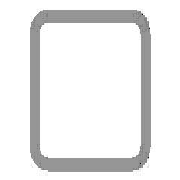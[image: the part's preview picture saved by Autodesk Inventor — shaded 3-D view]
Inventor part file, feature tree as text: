
AUTODESK INVENTOR PART (.ipt)
format: ipt  version: 2024 (Build 280153000, 153)  size: 137,216 bytes
history: native  units: mm (DEFAULTED — no unit token found)
features: other x4, plane x3, split x2, extrude x1, sketch x1
ambient origin geometry x8: Origin, YZ Plane, XZ Plane, XY Plane, X Axis, Y Axis, Z Axis, Center Point
bodies: Solid1 (feature_tree)
feature tree (11):
  parser-record x1  (decoder bookkeeping rows leaked as tree rows — omitted from the tree; the rows remain in map.json)
  other  "Driven Length"
  other  "Plano inicial"
  other  "Plano final"
  extrude  "Cuerpo"  TaperAngle=0.0deg  [1 undecoded]
  plane  "Plano de trabajo4"
  split  "Dividir1"
  plane  "Plano de trabajo5"
  split  "Dividir2"
  sketch  "Sketch3"  dims[d3=2039.2mm d4=0.0mm d10=50.8mm d11=50.8mm d12=3.175mm d13=25.4mm d14=2064.6mm d15=25.4mm d16=25.4mm d17=6.35mm d18=90.0deg d19=2039.2mm]
  plane  "Work Plane3"
note: 1 required parameter value undecoded (feature->parameter linkage not recoverable at this tier; creation-order binding heuristic only, values carry confidence <= 0.55)
